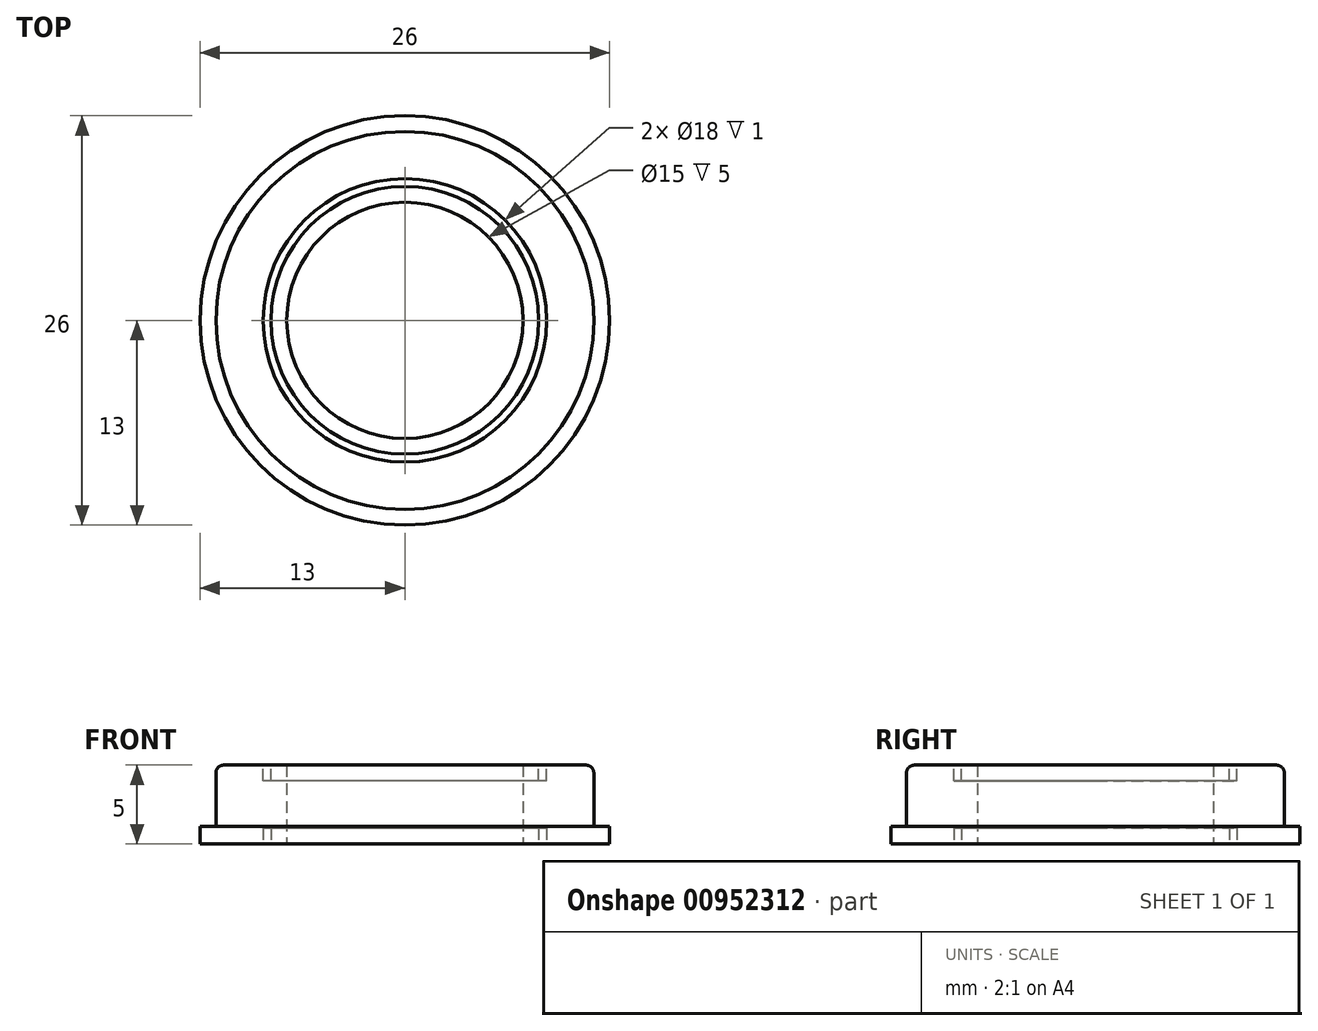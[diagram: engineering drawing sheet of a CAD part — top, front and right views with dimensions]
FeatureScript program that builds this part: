
annotation { "Feature Type Name" : "Feature", "Feature Type Description" : "" }
export const myFeature = defineFeature(function(context is Context, id is Id, definition is map)
    precondition{}
    {
        {
            var Q0;
            Q0=qCreatedBy(makeId("Top.planeOp"),FACE);
            var sketch = newSketch(context, id + "F0", { "sketchPlane" : qUnion([Q0])});
            skCircle(sketch, "E0", {"center": v(0, 0) * mm, "radius": 12 * mm});
            skCircle(sketch, "E1", {"center": v(0, 0) * mm, "radius": 7.5 * mm});
            skSolve(sketch);
        }
        {
            var Q0;
            Q0 = qSketchRegion(id + "F0", true);
            extrude(context, id + "F1", {"entities" : qUnion([Q0]), "depth" : 5 * mm, "offsetDistance" : 25 * mm, "symmetric" : true});
        }
        {
            var Q0;
            Q0=makeQuery(id+"F1.opExtrude","CAP_EDGE",EDGE,{"disambiguationData":[OSD([sQuery(id+"F0.wireOp",EDGE,"E0")])],"isStart":false});
            fillet(context, id + "F2", {"entities" : qUnion([Q0]), "radius" : 0.5 * mm, "tangentPropagation" : true, "allowEdgeOverflow" : false});
        }
        {
            var Q0;
            Q0=makeQuery(id+"F1.opExtrude","CAP_FACE",FACE,{"disambiguationData":[OSD([sQuery(id+"F0.wireOp",EDGE,"E0"),sQuery(id+"F0.wireOp",EDGE,"E1")])],"isStart":true});
            var sketch = newSketch(context, id + "F3", { "sketchPlane" : qUnion([Q0])});
            skCircle(sketch, "E2", {"center": v(0, 0) * mm, "radius": 13 * mm});
            skCircle(sketch, "E3", {"center": v(0, 0) * mm, "radius": 10 * mm});
            skSolve(sketch);
        }
        {
            var Q0;
            Q0 = qSketchRegion(id + "F3", true);
            extrude(context, id + "F4", {"entities" : qUnion([Q0]), "operationType" : NewBodyOperationType.ADD, "oppositeDirection" : true, "depth" : 1.1 * mm, "offsetDistance" : 25 * mm});
        }
        {
            var Q0;
            Q0=makeQuery(id+"F4.boolean.opBoolean","MERGE",FACE,{"derivedFrom":[makeQuery(id+"F1.opExtrude","CAP_FACE",FACE,{"disambiguationData":[OSD([sQuery(id+"F0.wireOp",EDGE,"E0"),sQuery(id+"F0.wireOp",EDGE,"E1")])],"isStart":true}),makeQuery(id+"F4.opExtrude","CAP_FACE",FACE,{"disambiguationData":[OSD([sQuery(id+"F3.wireOp",EDGE,"E2"),sQuery(id+"F3.wireOp",EDGE,"E3")])],"isStart":true})]});
            var sketch = newSketch(context, id + "F5", { "sketchPlane" : qUnion([Q0])});
            skCircle(sketch, "E4", {"center": v(0, 0) * mm, "radius": 8.5 * mm});
            skCircle(sketch, "E5", {"center": v(0, 0) * mm, "radius": 9 * mm});
            skSolve(sketch);
        }
        {
            var Q0;
            Q0 = qSketchRegion(id + "F5", true);
            extrude(context, id + "F6", {"entities" : qUnion([Q0]), "operationType" : NewBodyOperationType.REMOVE, "oppositeDirection" : true, "depth" : 1 * mm, "offsetDistance" : 25 * mm});
        }
        {
            var Q0;
            Q0=makeQuery(id+"F1.opExtrude","CAP_FACE",FACE,{"disambiguationData":[OSD([sQuery(id+"F0.wireOp",EDGE,"E0"),sQuery(id+"F0.wireOp",EDGE,"E1")])],"isStart":false});
            var sketch = newSketch(context, id + "F7", { "sketchPlane" : qUnion([Q0])});
            skCircle(sketch, "E6", {"center": v(0, 0) * mm, "radius": 8.5 * mm});
            skCircle(sketch, "E7", {"center": v(0, 0) * mm, "radius": 9 * mm});
            skSolve(sketch);
        }
        {
            var Q0;
            Q0 = qSketchRegion(id + "F7", true);
            extrude(context, id + "F8", {"entities" : qUnion([Q0]), "operationType" : NewBodyOperationType.REMOVE, "oppositeDirection" : true, "depth" : 1 * mm, "offsetDistance" : 25 * mm});
        }
    });
